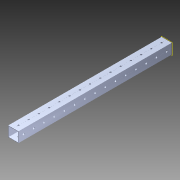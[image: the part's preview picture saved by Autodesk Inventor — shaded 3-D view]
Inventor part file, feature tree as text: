
AUTODESK INVENTOR PART (.ipt)
format: ipt  version: 2014 (Build 180170000, 170)  size: 1,194,496 bytes
history: native  units: in
note: dims shown in document units (in); Inventor stores cm internally (conversion verified against a paired STEP export)
features: pattern_circular x1, other x1, plane x1, extrude x1, imported_body x1, sketch x1
ambient origin geometry x8: Origin, YZ Plane, XZ Plane, XY Plane, X Axis, Y Axis, Z Axis, Center Point
bodies: Body1 (feature_tree)
feature tree (6):
  pattern_circular  "CirPattern2"
  other  "217-3426-STEP1"
  plane  "Work Plane1"
  extrude  "Extrusion1"  Depth=3937.0079in TaperAngle=0.0deg
  imported_body  "Base1"
  sketch  "Sketch1"  dims[d0=-15.0in d1=3937.0079in d2=0.0in]
